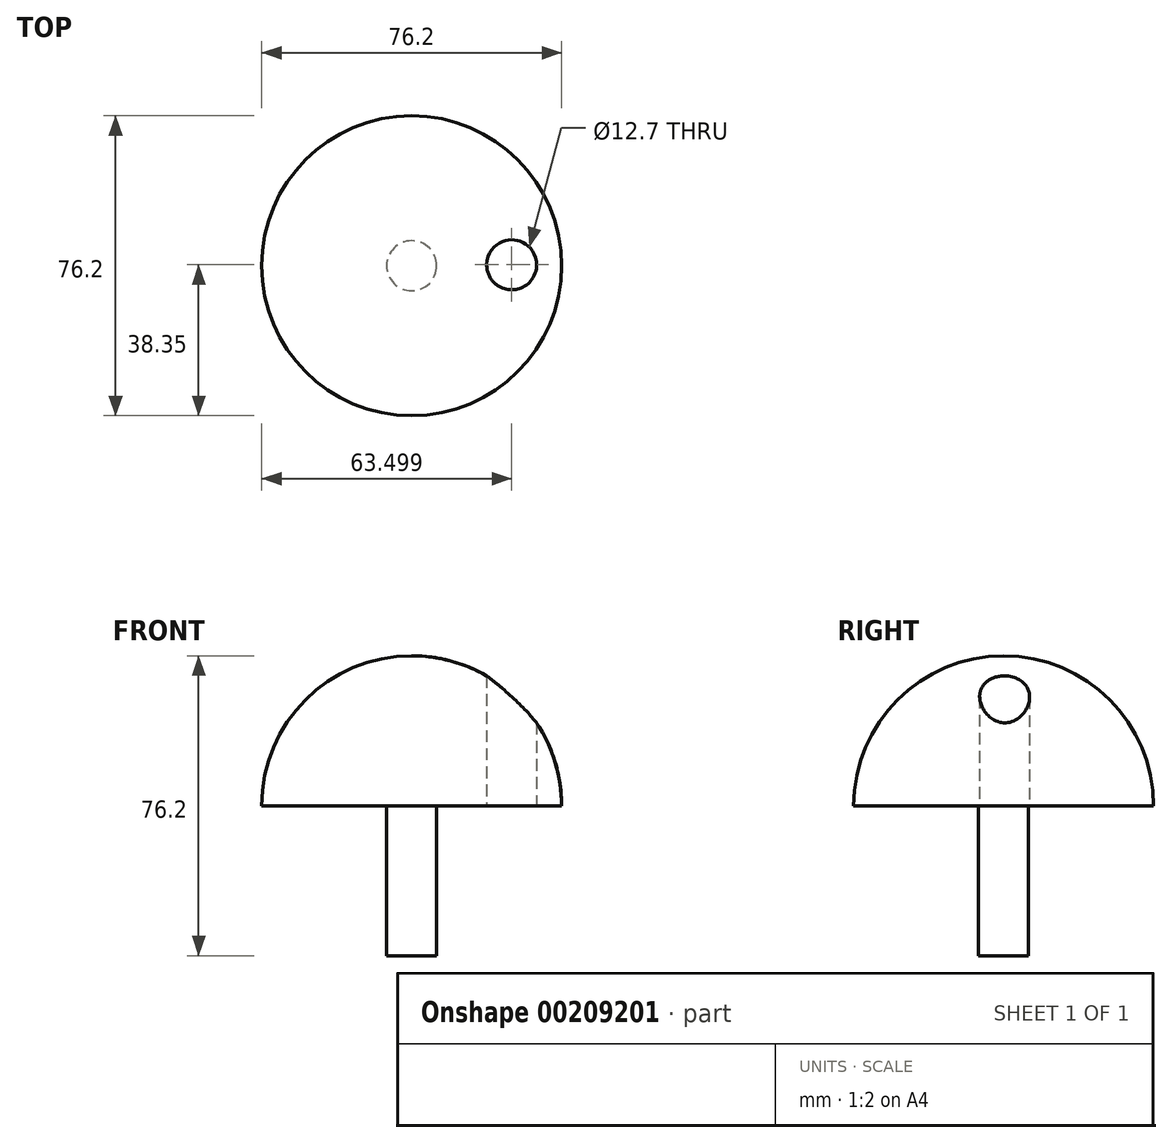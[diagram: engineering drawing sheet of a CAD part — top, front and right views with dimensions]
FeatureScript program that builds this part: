
annotation { "Feature Type Name" : "Feature", "Feature Type Description" : "" }
export const myFeature = defineFeature(function(context is Context, id is Id, definition is map)
    precondition{}
    {
        {
            var Q0;
            Q0=qCreatedBy(makeId("Front.planeOp"),FACE);
            var sketch = newSketch(context, id + "F0", { "sketchPlane" : qUnion([Q0])});
            skLineSegment(sketch, "E0", {"start": v(0, 0) * mm, "end": v(0, 76.2) * mm});
            skArc(sketch, "E1", {"start": v(0, 76.2) * mm, "mid": v(26.94, 65.04) * mm, "end": v(38.1, 38.1) * mm});
            skLineSegment(sketch, "E2", {"start": v(38.1, 38.1) * mm, "end": v(6.35, 38.1) * mm});
            skLineSegment(sketch, "E3", {"start": v(6.35, 38.1) * mm, "end": v(6.35, 0) * mm});
            skLineSegment(sketch, "E4", {"start": v(6.35, 0) * mm, "end": v(0, 0) * mm});
            skSolve(sketch);
        }
        {
            var Q0;
            Q0=makeQuery(id+"F0.imprint","IMPRINT",FACE,{"disambiguationData":[TD([[makeQuery(id+"F0.imprint","IMPRINT",EDGE,{"derivedFrom":sQuery(id+"F0.wireOp",EDGE,"E0")}),-1.0]])]});
            var Q1;
            Q1=sQuery(id+"F0.wireOp",EDGE,"E0");
            revolve(context, id + "F1", {"entities" : qUnion([Q0]), "axis" : qUnion([Q1]), "revolveType" : RevolveType.FULL});
        }
        {
            var Q0;
            Q0=makeQuery(id+"F1.opRevolve","SWEPT_FACE",FACE,{"disambiguationData":[OSD([sQuery(id+"F0.wireOp",EDGE,"E2")])]});
            var sketch = newSketch(context, id + "F2", { "sketchPlane" : qUnion([Q0])});
            skCircle(sketch, "E5", {"center": v(25.4, -0.25) * mm, "radius": 6.35 * mm});
            skSolve(sketch);
        }
        {
            var Q0;
            Q0=makeQuery(id+"F2.imprint","IMPRINT",FACE,{"disambiguationData":[TD([[makeQuery(id+"F2.imprint","IMPRINT",EDGE,{"derivedFrom":sQuery(id+"F2.wireOp",EDGE,"E5")}),1.0]])]});
            extrude(context, id + "F3", {"entities" : qUnion([Q0]), "operationType" : NewBodyOperationType.REMOVE, "oppositeDirection" : true, "depth" : 50.8 * mm});
        }
    });
